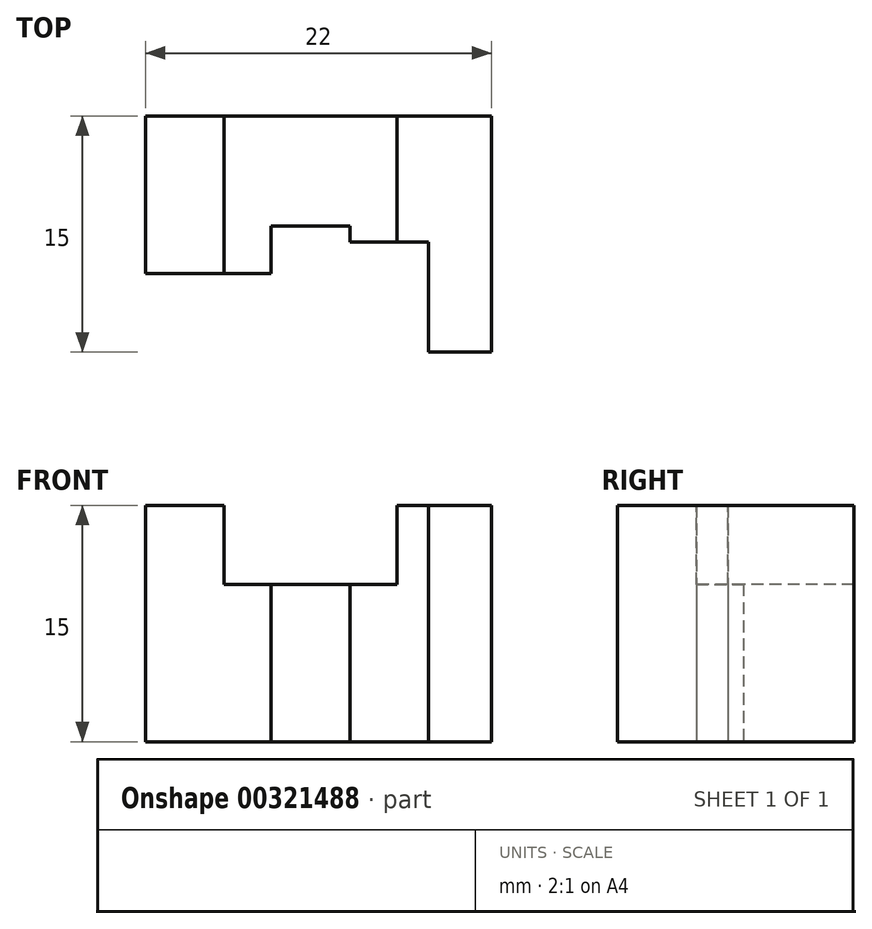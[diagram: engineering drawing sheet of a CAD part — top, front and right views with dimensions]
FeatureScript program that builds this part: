
annotation { "Feature Type Name" : "Feature", "Feature Type Description" : "" }
export const myFeature = defineFeature(function(context is Context, id is Id, definition is map)
    precondition{}
    {
        {
            var Q0;
            Q0=qCreatedBy(makeId("Top.planeOp"),FACE);
            var sketch = newSketch(context, id + "F0", { "sketchPlane" : qUnion([Q0])});
            skLineSegment(sketch, "E0", {"start": v(0, 0) * mm, "end": v(0, 10) * mm});
            skLineSegment(sketch, "E1", {"start": v(0, 10) * mm, "end": v(22, 10) * mm});
            skLineSegment(sketch, "E2", {"start": v(22, 10) * mm, "end": v(22, -5) * mm});
            skLineSegment(sketch, "E3", {"start": v(22, -5) * mm, "end": v(18, -5) * mm});
            skLineSegment(sketch, "E4", {"start": v(18, -5) * mm, "end": v(18, 0) * mm});
            skLineSegment(sketch, "E5", {"start": v(8, 0) * mm, "end": v(0, 0) * mm});
            skLineSegment(sketch, "E6", {"start": v(8, 0) * mm, "end": v(8, 3) * mm});
            skLineSegment(sketch, "E7", {"start": v(8, 3) * mm, "end": v(13, 3) * mm});
            skLineSegment(sketch, "E8", {"start": v(13, 3) * mm, "end": v(13, 2) * mm});
            skLineSegment(sketch, "E9", {"start": v(13, 2) * mm, "end": v(18, 2) * mm});
            skLineSegment(sketch, "E10", {"start": v(18, 2) * mm, "end": v(18, 0) * mm});
            skSolve(sketch);
        }
        {
            var Q0;
            Q0 = qSketchRegion(id + "F0", true);
            extrude(context, id + "F1", {"entities" : qUnion([Q0]), "depth" : 15 * mm});
        }
        {
            var Q0;
            Q0=makeQuery(id+"F1.opExtrude","CAP_FACE",FACE,{"disambiguationData":[OSD([sQuery(id+"F0.wireOp",EDGE,"E0"),sQuery(id+"F0.wireOp",EDGE,"E1"),sQuery(id+"F0.wireOp",EDGE,"E2"),sQuery(id+"F0.wireOp",EDGE,"E3"),sQuery(id+"F0.wireOp",EDGE,"E4"),sQuery(id+"F0.wireOp",EDGE,"E5"),sQuery(id+"F0.wireOp",EDGE,"E6"),sQuery(id+"F0.wireOp",EDGE,"E7"),sQuery(id+"F0.wireOp",EDGE,"E8"),sQuery(id+"F0.wireOp",EDGE,"E9"),sQuery(id+"F0.wireOp",EDGE,"E10")])],"isStart":false});
            var sketch = newSketch(context, id + "F2", { "sketchPlane" : qUnion([Q0])});
            skLineSegment(sketch, "E11", {"start": v(16, 10) * mm, "end": v(16, 2) * mm});
            skLineSegment(sketch, "E12", {"start": v(5, 10) * mm, "end": v(5, 0) * mm});
            skLineSegment(sketch, "E13", {"start": v(5, 0) * mm, "end": v(8, 0) * mm});
            skLineSegment(sketch, "E14", {"start": v(8, 0) * mm, "end": v(8, 3) * mm});
            skLineSegment(sketch, "E15", {"start": v(8, 3) * mm, "end": v(13, 3) * mm});
            skLineSegment(sketch, "E16", {"start": v(13, 3) * mm, "end": v(13, 2) * mm});
            skLineSegment(sketch, "E17", {"start": v(13, 2) * mm, "end": v(16, 2) * mm});
            skLineSegment(sketch, "E18", {"start": v(5, 10) * mm, "end": v(16, 10) * mm});
            skSolve(sketch);
        }
        {
            var Q0;
            Q0 = qSketchRegion(id + "F2", true);
            extrude(context, id + "F3", {"entities" : qUnion([Q0]), "operationType" : NewBodyOperationType.REMOVE, "oppositeDirection" : true, "depth" : 5 * mm});
        }
    });
